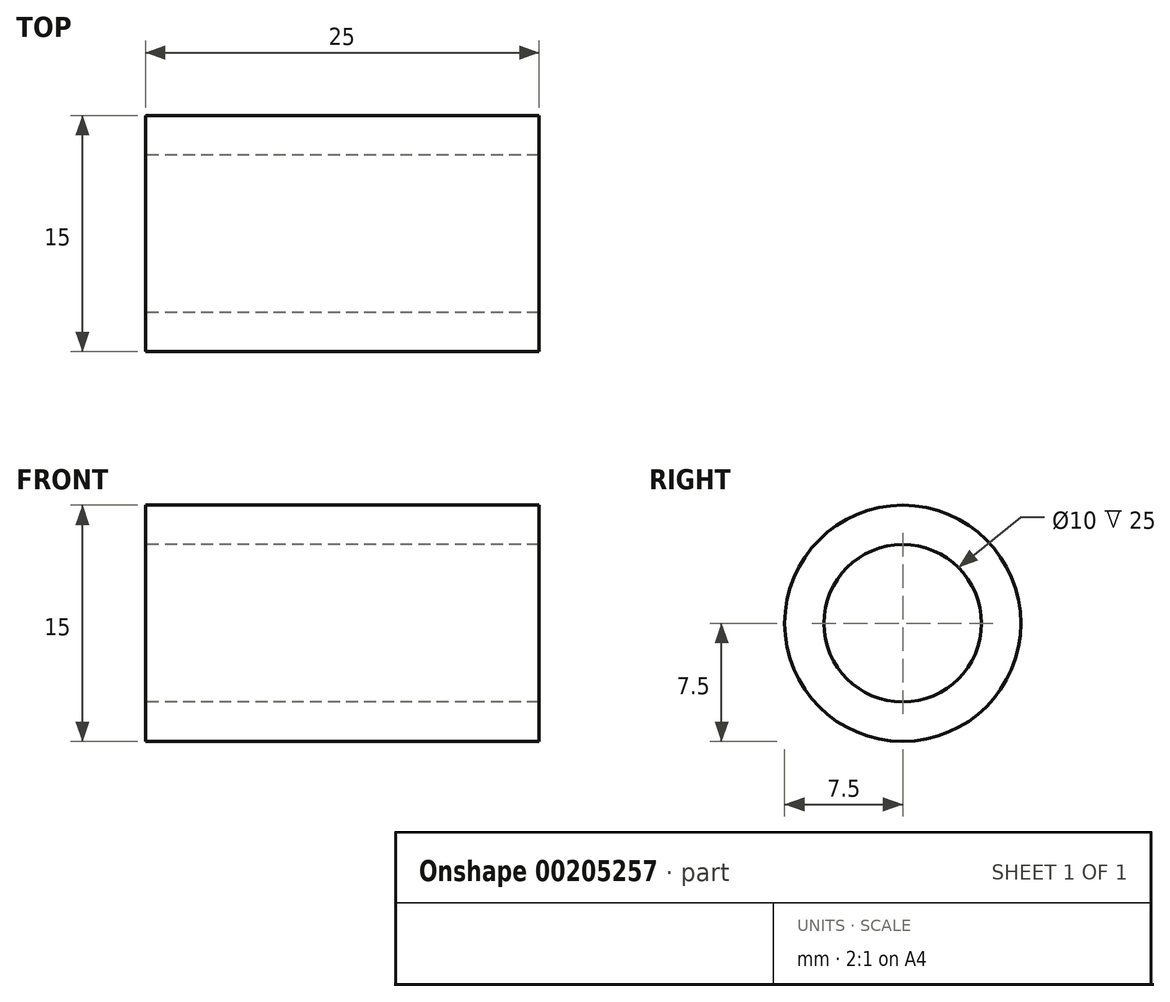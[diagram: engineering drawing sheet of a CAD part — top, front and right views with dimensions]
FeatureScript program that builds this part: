
annotation { "Feature Type Name" : "Feature", "Feature Type Description" : "" }
export const myFeature = defineFeature(function(context is Context, id is Id, definition is map)
    precondition{}
    {
        {
            var Q0;
            Q0=qCreatedBy(makeId("Right.planeOp"),FACE);
            var sketch = newSketch(context, id + "F0", { "sketchPlane" : qUnion([Q0])});
            skCircle(sketch, "E0", {"center": v(0, 0) * mm, "radius": 7.5 * mm});
            skSolve(sketch);
        }
        {
            var Q0;
            Q0=makeQuery(id+"F0.imprint","IMPRINT",FACE,{"disambiguationData":[TD([[makeQuery(id+"F0.imprint","IMPRINT",EDGE,{"derivedFrom":sQuery(id+"F0.wireOp",EDGE,"E0")}),1.0]])]});
            var sketch = newSketch(context, id + "F1", { "sketchPlane" : qUnion([Q0])});
            skCircle(sketch, "E1", {"center": v(0, 0) * mm, "radius": 5 * mm});
            skSolve(sketch);
        }
        {
            var Q0;
            Q0=makeQuery(id+"F0.imprint","IMPRINT",FACE,{"disambiguationData":[TD([[makeQuery(id+"F0.imprint","IMPRINT",EDGE,{"derivedFrom":sQuery(id+"F0.wireOp",EDGE,"E0")}),1.0]])]});
            var Q1;
            Q1=sQuery(id+"F0.wireOp",EDGE,"E0");
            extrude(context, id + "F2", {"entities" : qUnion([Q0]), "surfaceEntities" : qUnion([Q1]), "depth" : 25 * mm});
        }
        {
            var Q0;
            Q0=makeQuery(id+"F1.imprint","IMPRINT",FACE,{"disambiguationData":[TD([[makeQuery(id+"F1.imprint","IMPRINT",EDGE,{"derivedFrom":sQuery(id+"F1.wireOp",EDGE,"E1")}),1.0]])]});
            extrude(context, id + "F3", {"entities" : qUnion([Q0]), "operationType" : NewBodyOperationType.REMOVE, "depth" : 25 * mm});
        }
    });
